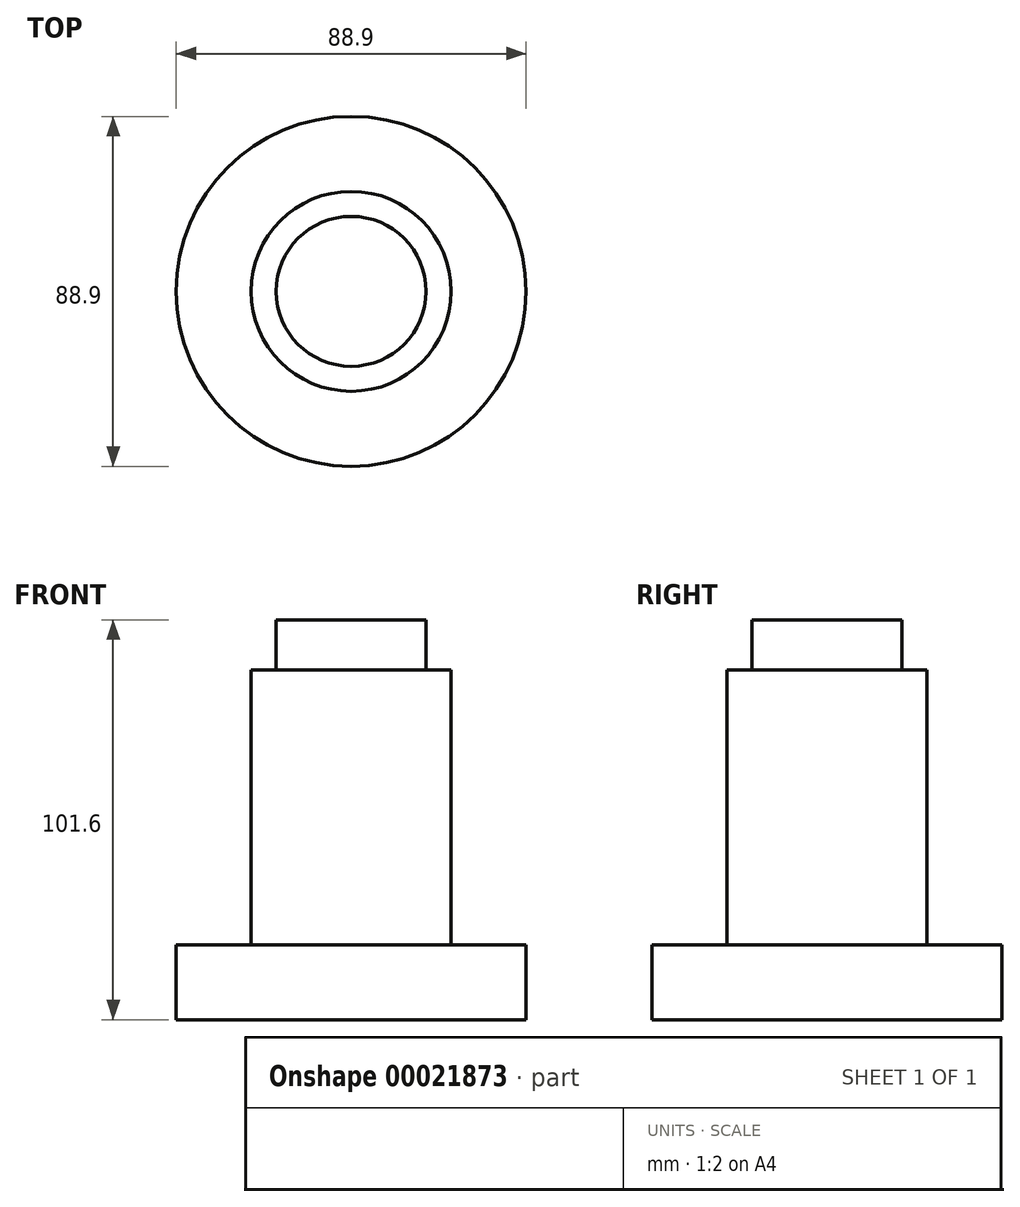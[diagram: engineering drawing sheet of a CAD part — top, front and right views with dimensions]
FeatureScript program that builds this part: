
annotation { "Feature Type Name" : "Feature", "Feature Type Description" : "" }
export const myFeature = defineFeature(function(context is Context, id is Id, definition is map)
    precondition{}
    {
        {
            var Q0;
            Q0=qCreatedBy(makeId("Front.planeOp"),FACE);
            var sketch = newSketch(context, id + "F0", { "sketchPlane" : qUnion([Q0])});
            skLineSegment(sketch, "E0", {"start": v(11.45, -16) * mm, "end": v(55.9, -16) * mm});
            skLineSegment(sketch, "E1", {"start": v(55.9, -16) * mm, "end": v(55.9, 3.05) * mm});
            skLineSegment(sketch, "E2", {"start": v(55.9, 3.05) * mm, "end": v(36.85, 3.05) * mm});
            skLineSegment(sketch, "E3", {"start": v(36.85, 3.05) * mm, "end": v(36.85, 72.9) * mm});
            skLineSegment(sketch, "E4", {"start": v(30.5, 72.9) * mm, "end": v(30.5, 85.6) * mm});
            skLineSegment(sketch, "E5", {"start": v(30.5, 85.6) * mm, "end": v(11.45, 85.6) * mm});
            skLineSegment(sketch, "E6", {"start": v(11.45, 85.6) * mm, "end": v(11.45, -16) * mm});
            skLineSegment(sketch, "E7", {"start": v(11.45, 96.51) * mm, "end": v(11.45, 46.82) * mm});
            skLineSegment(sketch, "E8", {"start": v(30.5, 72.9) * mm, "end": v(36.85, 72.9) * mm});
            skSolve(sketch);
        }
        {
            var Q0;
            Q0=makeQuery(id+"F0.imprint","IMPRINT",FACE,{"disambiguationData":[TD([[makeQuery(id+"F0.imprint","IMPRINT",EDGE,{"derivedFrom":sQuery(id+"F0.wireOp",EDGE,"E0")}),1.0]])]});
            var Q1;
            Q1=sQuery(id+"F0.wireOp",EDGE,"E7");
            revolve(context, id + "F1", {"entities" : qUnion([Q0]), "axis" : qUnion([Q1]), "revolveType" : RevolveType.FULL});
        }
    });
